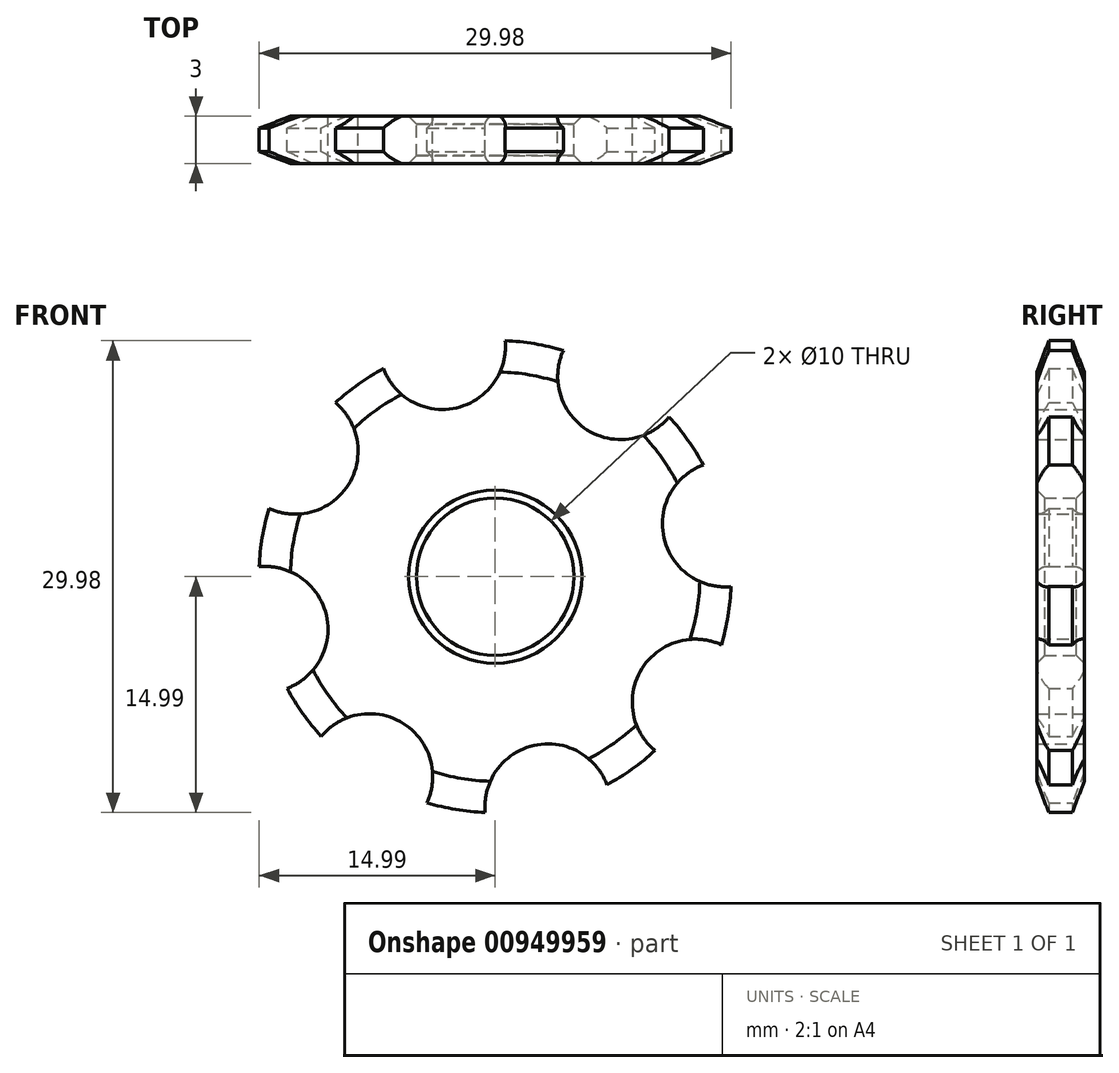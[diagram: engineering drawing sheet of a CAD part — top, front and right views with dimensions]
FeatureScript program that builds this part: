
annotation { "Feature Type Name" : "Feature", "Feature Type Description" : "" }
export const myFeature = defineFeature(function(context is Context, id is Id, definition is map)
    precondition{}
    {
        {
            var Q0;
            Q0=qCreatedBy(makeId("Front.planeOp"),FACE);
            var sketch = newSketch(context, id + "F0", { "sketchPlane" : qUnion([Q0])});
            skCircle(sketch, "E0", {"center": v(0, 0) * mm, "radius": 15 * mm});
            skCircle(sketch, "E1", {"center": v(-12.7, 7.97) * mm, "radius": 4 * mm});
            skCircle(sketch, "E2.1.0", {"center": v(-14.62, -3.35) * mm, "radius": 4 * mm});
            skCircle(sketch, "E2.2.0", {"center": v(-7.97, -12.7) * mm, "radius": 4 * mm});
            skCircle(sketch, "E2.3.0", {"center": v(3.35, -14.62) * mm, "radius": 4 * mm});
            skCircle(sketch, "E2.4.0", {"center": v(12.7, -7.97) * mm, "radius": 4 * mm});
            skCircle(sketch, "E2.5.0", {"center": v(14.62, 3.35) * mm, "radius": 4 * mm});
            skCircle(sketch, "E2.6.0", {"center": v(7.97, 12.7) * mm, "radius": 4 * mm});
            skCircle(sketch, "E2.7.0", {"center": v(-3.35, 14.62) * mm, "radius": 4 * mm});
            skCircle(sketch, "E3", {"center": v(0, 0) * mm, "radius": 5 * mm});
            skSolve(sketch);
        }
        {
            var Q0;
            Q0=makeQuery(id+"F0.imprint","IMPRINT",FACE,{"disambiguationData":[TD([[makeQuery(id+"F0.imprint","IMPRINT",EDGE,{"derivedFrom":sQuery(id+"F0.wireOp",EDGE,"E0")}),1.0]])]});
            extrude(context, id + "F1", {"entities" : qUnion([Q0]), "depth" : 3 * mm, "offsetDistance" : 25 * mm});
        }
        {
            var Q0;
            {var subQ0=sQuery(id+"F0.wireOp",EDGE,"E0");Q0=makeQuery(id+"FjPS6zSCau8WYdw_1.boolean.opBoolean","SPLIT",EDGE,{"disambiguationData":[TD([makeQuery(id+"F1.opExtrude","SWEPT_FACE",FACE,{"disambiguationData":[OSD([subQ0])]}),makeQuery(id+"F1.opExtrude","CAP_FACE",FACE,{"disambiguationData":[OSD([subQ0])],"isStart":false}),makeQuery(id+"FjPS6zSCau8WYdw_1.opExtrude","SWEPT_FACE",FACE,{"disambiguationData":[OSD([sQuery(id+"FptURnvkRjZK9U8_1.wireOp",EDGE,"c81c12ed-b287-469f-bd1e-95274906ad68.5.0")])]}),makeQuery(id+"FjPS6zSCau8WYdw_1.opExtrude","SWEPT_FACE",FACE,{"disambiguationData":[OSD([sQuery(id+"FptURnvkRjZK9U8_1.wireOp",EDGE,"c81c12ed-b287-469f-bd1e-95274906ad68.6.0")])]})])],"derivedFrom":makeQuery(id+"F1.opExtrude","CAP_EDGE",EDGE,{"disambiguationData":[OSD([subQ0])],"isStart":false})});}
            chamfer(context, id + "F2", {"entities" : qUnion([Q0]), "chamferType" : ChamferType.TWO_OFFSETS, "width1" : 2 * mm, "oppositeDirection" : false, "width2" : 0.75 * mm, "tangentPropagation" : true});
        }
        {
            var Q0;
            {var subQ0=sQuery(id+"F0.wireOp",EDGE,"E0");Q0=makeQuery(id+"FjPS6zSCau8WYdw_1.boolean.opBoolean","SPLIT",EDGE,{"disambiguationData":[TD([makeQuery(id+"F1.opExtrude","SWEPT_FACE",FACE,{"disambiguationData":[OSD([subQ0])]}),makeQuery(id+"F1.opExtrude","CAP_FACE",FACE,{"disambiguationData":[OSD([subQ0])],"isStart":true}),makeQuery(id+"FjPS6zSCau8WYdw_1.opExtrude","SWEPT_FACE",FACE,{"disambiguationData":[OSD([sQuery(id+"FptURnvkRjZK9U8_1.wireOp",EDGE,"c81c12ed-b287-469f-bd1e-95274906ad68.21.0")])]}),makeQuery(id+"FjPS6zSCau8WYdw_1.opExtrude","SWEPT_FACE",FACE,{"disambiguationData":[OSD([sQuery(id+"FptURnvkRjZK9U8_1.wireOp",EDGE,"c81c12ed-b287-469f-bd1e-95274906ad68.22.0")])]})])],"derivedFrom":makeQuery(id+"F1.opExtrude","CAP_EDGE",EDGE,{"disambiguationData":[OSD([subQ0])],"isStart":true})});}
            chamfer(context, id + "F3", {"entities" : qUnion([Q0]), "chamferType" : ChamferType.TWO_OFFSETS, "width1" : 0.75 * mm, "oppositeDirection" : false, "width2" : 2 * mm, "tangentPropagation" : true});
        }
        {
            var Q0;
            Q0=makeQuery(id+"F1.opExtrude","CAP_EDGE",EDGE,{"disambiguationData":[OSD([sQuery(id+"F0.wireOp",EDGE,"E3")])],"isStart":false});
            var Q1;
            Q1=makeQuery(id+"F1.opExtrude","CAP_EDGE",EDGE,{"disambiguationData":[OSD([sQuery(id+"F0.wireOp",EDGE,"E3")])],"isStart":true});
            chamfer(context, id + "F4", {"entities" : qUnion([Q0, Q1]), "width" : 0.5 * mm, "tangentPropagation" : true});
        }
    });
